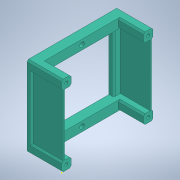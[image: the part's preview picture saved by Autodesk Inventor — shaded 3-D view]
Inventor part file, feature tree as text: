
AUTODESK INVENTOR PART (.ipt)
format: ipt  version: 2020 (Build 240168000, 168)  size: 211,456 bytes
history: native  units: mm
features: sketch x6, extrude x5, pattern_linear x1, chamfer x1
ambient origin geometry x8: Origin, YZ Plane, XZ Plane, XY Plane, X Axis, Y Axis, Z Axis, Center Point
bodies: Solid1 (feature_tree)
feature tree (13):
  extrude  "Extrusion1"  Depth=6.0mm
  extrude  "Extrusion2"  Depth=22.0mm
  extrude  "Extrusion3"  Depth=6.0mm
  pattern_linear  "Rectangular Pattern2"  Count1=2 Spacing1=45.0mm
  extrude  "Extrusion4"  Depth=3.0mm TaperAngle=0.0deg
  chamfer  "Chamfer3"  Distance=1.0mm Angle=45.0deg
  sketch  "Sketch6"  dims[d9=3.0mm]
  extrude  "Extrusion5"  Depth=0.8mm
  sketch  "Sketch1"  dims[d0=6.0mm d1=6.0mm]
  sketch  "Sketch2"  dims[d2=58.0mm d3=22.0mm]
  sketch  "Sketch3"  dims[d4=6.0mm d5=0.0mm d6=2.0mm]
  sketch  "Sketch5"  dims[d7=12.0mm d8=0.0mm]
  sketch  "Sketch7"  dims[d10=0.0mm d11=0.0mm d21=20.0mm d23=45.0mm d24=3.0mm d25=0.0mm d26=1.0mm d27=2.0mm d28=45.0deg d29=0.8mm d30=0.8mm d31=3.0mm d32=0.0mm]
